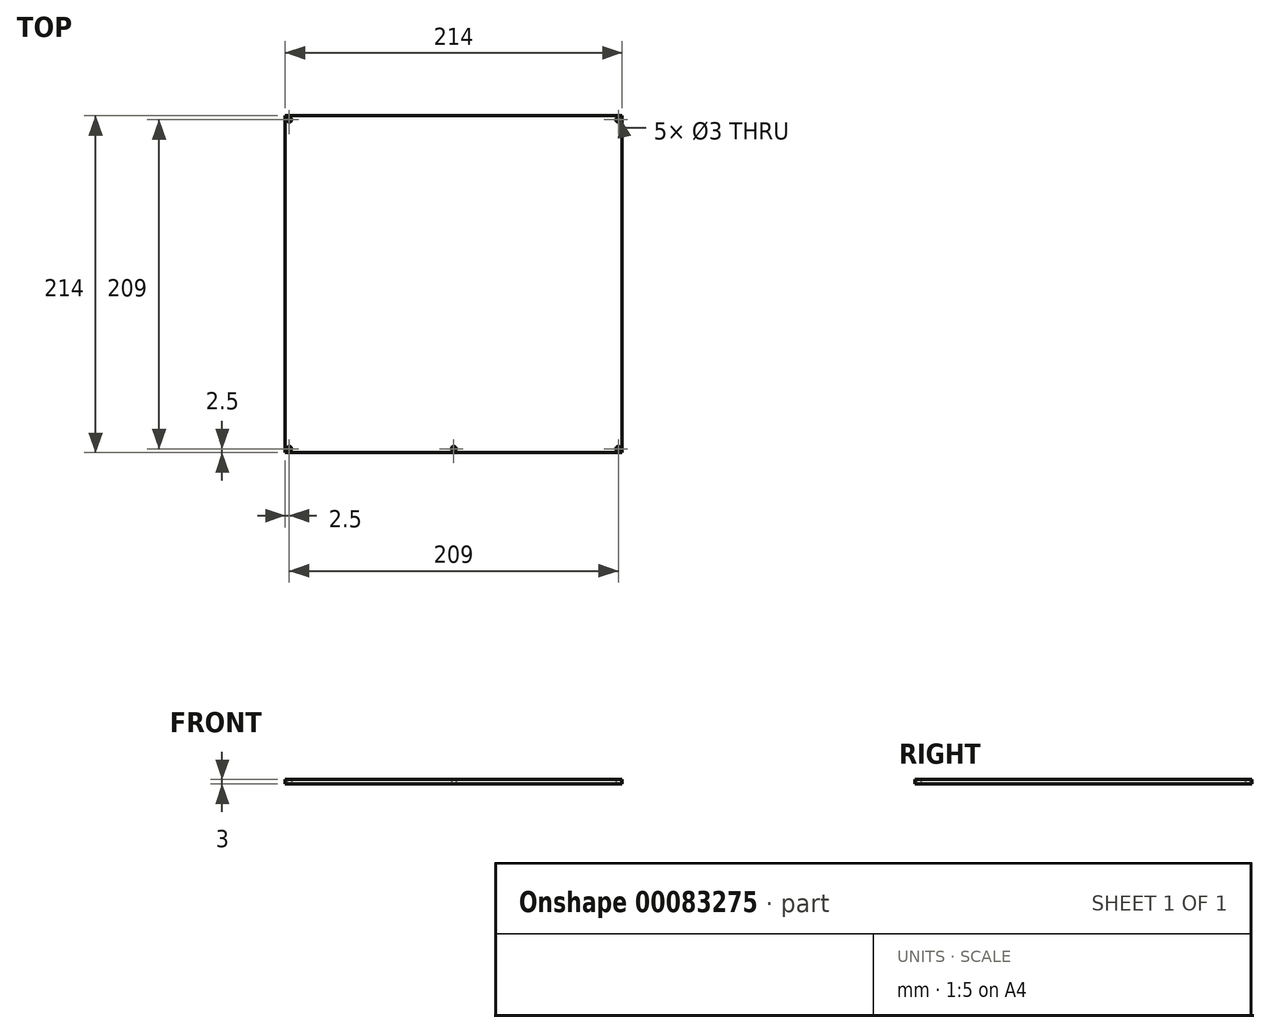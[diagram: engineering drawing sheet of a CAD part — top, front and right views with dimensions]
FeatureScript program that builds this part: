
annotation { "Feature Type Name" : "Feature", "Feature Type Description" : "" }
export const myFeature = defineFeature(function(context is Context, id is Id, definition is map)
    precondition{}
    {
        {
            var Q0;
            Q0=qCreatedBy(makeId("Top.planeOp"),FACE);
            var sketch = newSketch(context, id + "F0", { "sketchPlane" : qUnion([Q0])});
            skLineSegment(sketch, "E0.bottom", {"start": v(107, 107) * mm, "end": v(-107, 107) * mm});
            skLineSegment(sketch, "E0.top", {"start": v(107, -107) * mm, "end": v(-107, -107) * mm});
            skLineSegment(sketch, "E0.left", {"start": v(107, 107) * mm, "end": v(107, -107) * mm});
            skLineSegment(sketch, "E0.right", {"start": v(-107, 107) * mm, "end": v(-107, -107) * mm});
            skPoint(sketch, "E0.middle", {"position": v(0, 0) * mm});
            skLineSegment(sketch, "E1.bottom", {"start": v(104.5, 104.5) * mm, "end": v(-104.5, 104.5) * mm, "construction": true});
            skLineSegment(sketch, "E1.top", {"start": v(104.5, -104.5) * mm, "end": v(-104.5, -104.5) * mm, "construction": true});
            skLineSegment(sketch, "E1.left", {"start": v(104.5, 104.5) * mm, "end": v(104.5, -104.5) * mm, "construction": true});
            skLineSegment(sketch, "E1.right", {"start": v(-104.5, 104.5) * mm, "end": v(-104.5, -104.5) * mm, "construction": true});
            skCircle(sketch, "E2", {"center": v(-104.5, 104.5) * mm, "radius": 1.5 * mm});
            skCircle(sketch, "E3", {"center": v(104.5, 104.5) * mm, "radius": 1.5 * mm});
            skCircle(sketch, "E4", {"center": v(-104.5, -104.5) * mm, "radius": 1.5 * mm});
            skCircle(sketch, "E5", {"center": v(104.5, -104.5) * mm, "radius": 1.5 * mm});
            skCircle(sketch, "E6", {"center": v(0, -104.5) * mm, "radius": 1.5 * mm});
            skSolve(sketch);
        }
        {
            var Q0;
            Q0 = qSketchRegion(id + "F0", true);
            extrude(context, id + "F1", {"entities" : qUnion([Q0]), "depth" : 3 * mm});
        }
    });
